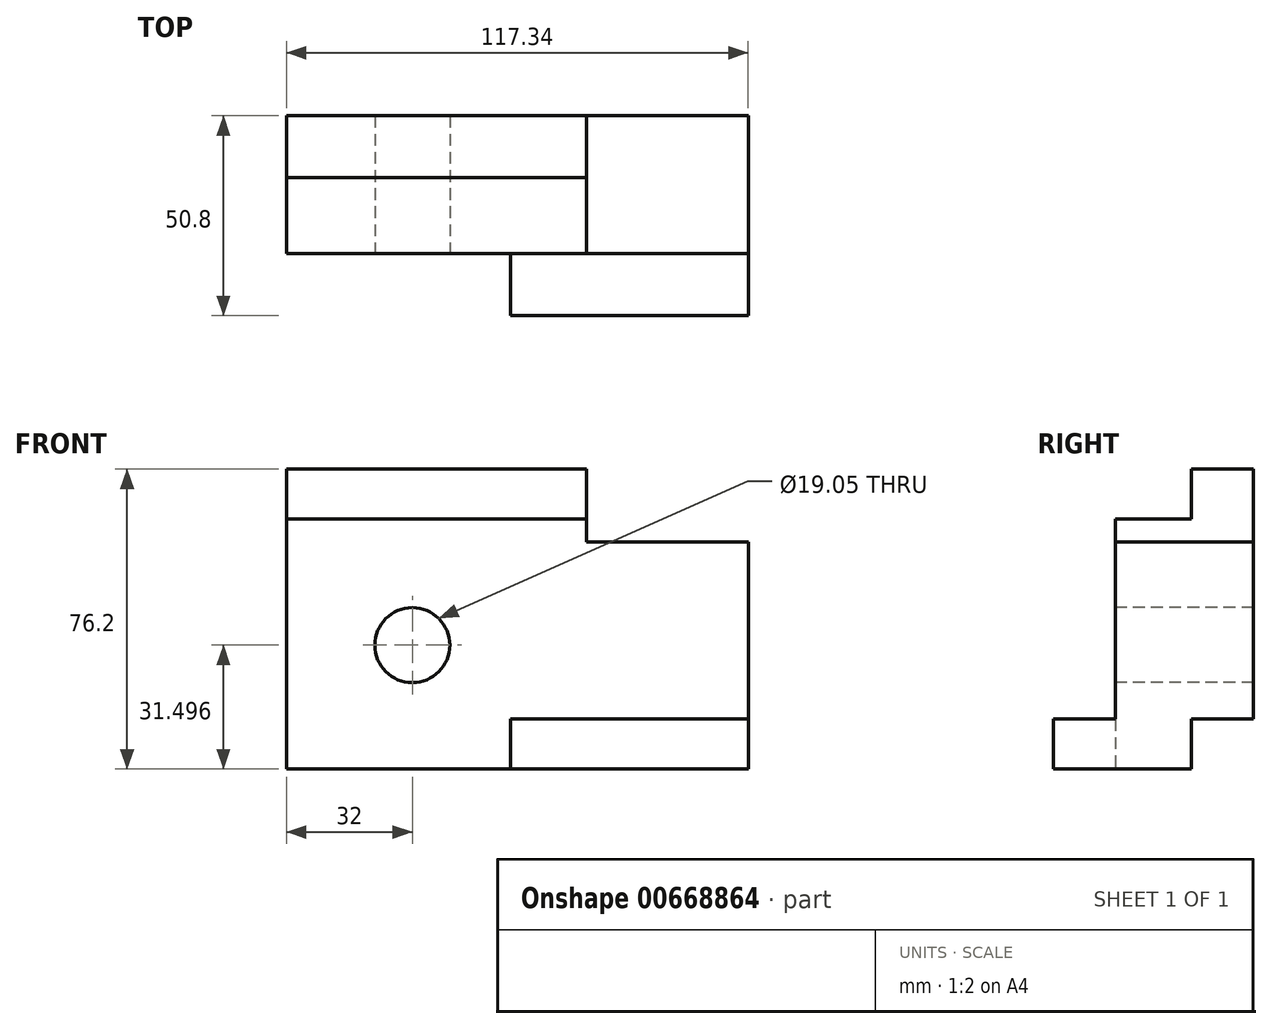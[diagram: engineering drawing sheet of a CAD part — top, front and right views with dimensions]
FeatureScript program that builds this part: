
annotation { "Feature Type Name" : "Feature", "Feature Type Description" : "" }
export const myFeature = defineFeature(function(context is Context, id is Id, definition is map)
    precondition{}
    {
        {
            var Q0;
            Q0=qCreatedBy(makeId("Front.planeOp"),FACE);
            var sketch = newSketch(context, id + "F0", { "sketchPlane" : qUnion([Q0])});
            skLineSegment(sketch, "E0.bottom", {"start": v(-58.67, 31.75) * mm, "end": v(58.67, 31.75) * mm});
            skLineSegment(sketch, "E0.top", {"start": v(-58.67, -31.75) * mm, "end": v(58.67, -31.75) * mm});
            skLineSegment(sketch, "E0.left", {"start": v(-58.67, 31.75) * mm, "end": v(-58.67, -31.75) * mm});
            skLineSegment(sketch, "E0.right", {"start": v(58.67, 31.75) * mm, "end": v(58.67, -31.75) * mm});
            skPoint(sketch, "E0.middle", {"position": v(0, 0) * mm});
            skSolve(sketch);
        }
        {
            var Q0;
            Q0=makeQuery(id+"F0.imprint","IMPRINT",FACE,{"disambiguationData":[TD([[makeQuery(id+"F0.imprint","IMPRINT",EDGE,{"derivedFrom":sQuery(id+"F0.wireOp",EDGE,"E0.bottom")}),-1.0]])]});
            extrude(context, id + "F1", {"entities" : qUnion([Q0]), "depth" : 35.05 * mm, "offsetDistance" : 25.4 * mm});
        }
        {
            var Q0;
            Q0=makeQuery(id+"F1.opExtrude","SWEPT_FACE",FACE,{"disambiguationData":[OSD([sQuery(id+"F0.wireOp",EDGE,"E0.bottom")])]});
            var sketch = newSketch(context, id + "F2", { "sketchPlane" : qUnion([Q0])});
            skLineSegment(sketch, "E1.bottom", {"start": v(-58.67, 0) * mm, "end": v(58.67, 0) * mm});
            skLineSegment(sketch, "E1.top", {"start": v(-58.67, -15.75) * mm, "end": v(58.67, -15.75) * mm});
            skLineSegment(sketch, "E1.left", {"start": v(-58.67, 0) * mm, "end": v(-58.67, -15.75) * mm});
            skLineSegment(sketch, "E1.right", {"start": v(58.67, 0) * mm, "end": v(58.67, -15.75) * mm});
            skSolve(sketch);
        }
        {
            var Q0;
            Q0=makeQuery(id+"F2.imprint","IMPRINT",FACE,{"disambiguationData":[TD([[makeQuery(id+"F2.imprint","IMPRINT",EDGE,{"derivedFrom":sQuery(id+"F2.wireOp",EDGE,"E1.bottom")}),-1.0]])]});
            extrude(context, id + "F3", {"entities" : qUnion([Q0]), "operationType" : NewBodyOperationType.ADD, "depth" : 12.7 * mm, "offsetDistance" : 25.4 * mm});
        }
        {
            var Q0;
            Q0=makeQuery(id+"F3.opExtrude","CAP_FACE",FACE,{"disambiguationData":[OSD([sQuery(id+"F2.wireOp",EDGE,"E1.bottom"),sQuery(id+"F2.wireOp",EDGE,"E1.top"),sQuery(id+"F2.wireOp",EDGE,"E1.left"),sQuery(id+"F2.wireOp",EDGE,"E1.right")])],"isStart":false});
            var sketch = newSketch(context, id + "F4", { "sketchPlane" : qUnion([Q0])});
            skLineSegment(sketch, "E2.bottom", {"start": v(58.67, 0) * mm, "end": v(17.53, 0) * mm});
            skLineSegment(sketch, "E2.top", {"start": v(58.67, -35.05) * mm, "end": v(17.53, -35.05) * mm});
            skLineSegment(sketch, "E2.left", {"start": v(58.67, 0) * mm, "end": v(58.67, -35.05) * mm});
            skLineSegment(sketch, "E2.right", {"start": v(17.53, 0) * mm, "end": v(17.53, -35.05) * mm});
            skSolve(sketch);
        }
        {
            var Q0;
            {var subQ0=sQuery(id+"F4.wireOp",EDGE,"E2.bottom");Q0=makeQuery(id+"F4.imprint","IMPRINT",FACE,{"disambiguationData":[TD([[makeQuery(id+"F4.imprint","IMPRINT",EDGE,{"derivedFrom":subQ0}),-1.0]])]});}
            var Q1;
            {var subQ0=sQuery(id+"F4.wireOp",EDGE,"E2.top");Q1=makeQuery(id+"F4.imprint","IMPRINT",FACE,{"disambiguationData":[TD([[makeQuery(id+"F4.imprint","IMPRINT",EDGE,{"derivedFrom":subQ0}),-1.0]])]});}
            extrude(context, id + "F5", {"entities" : qUnion([Q0, Q1]), "operationType" : NewBodyOperationType.REMOVE, "oppositeDirection" : true, "depth" : 18.44 * mm, "offsetDistance" : 25.4 * mm});
        }
        {
            var Q0;
            Q0=makeQuery(id+"F3.boolean.opBoolean","MERGE",FACE,{"derivedFrom":[makeQuery(id+"F1.opExtrude","SWEPT_FACE",FACE,{"disambiguationData":[OSD([sQuery(id+"F0.wireOp",EDGE,"E0.right")])]}),makeQuery(id+"F3.opExtrude","SWEPT_FACE",FACE,{"disambiguationData":[OSD([sQuery(id+"F2.wireOp",EDGE,"E1.right")])]})]});
            var sketch = newSketch(context, id + "F6", { "sketchPlane" : qUnion([Q0])});
            skLineSegment(sketch, "E3.bottom", {"start": v(0, -31.75) * mm, "end": v(-15.75, -31.75) * mm});
            skLineSegment(sketch, "E3.top", {"start": v(0, -19.05) * mm, "end": v(-15.75, -19.05) * mm});
            skLineSegment(sketch, "E3.left", {"start": v(0, -31.75) * mm, "end": v(0, -19.05) * mm});
            skLineSegment(sketch, "E3.right", {"start": v(-15.75, -31.75) * mm, "end": v(-15.75, -19.05) * mm});
            skSolve(sketch);
        }
        {
            var Q0;
            Q0=makeQuery(id+"F6.imprint","IMPRINT",FACE,{"disambiguationData":[TD([[makeQuery(id+"F6.imprint","IMPRINT",EDGE,{"derivedFrom":sQuery(id+"F6.wireOp",EDGE,"E3.bottom")}),1.0]])]});
            extrude(context, id + "F7", {"entities" : qUnion([Q0]), "operationType" : NewBodyOperationType.REMOVE, "endBound" : BoundingType.THROUGH_ALL, "oppositeDirection" : true, "depth" : 25.4 * mm, "offsetDistance" : 25.4 * mm});
        }
        {
            var Q0;
            Q0=makeQuery(id+"F3.boolean.opBoolean","MERGE",FACE,{"derivedFrom":[makeQuery(id+"F1.opExtrude","SWEPT_FACE",FACE,{"disambiguationData":[OSD([sQuery(id+"F0.wireOp",EDGE,"E0.right")])]}),makeQuery(id+"F3.opExtrude","SWEPT_FACE",FACE,{"disambiguationData":[OSD([sQuery(id+"F2.wireOp",EDGE,"E1.right")])]})]});
            var sketch = newSketch(context, id + "F8", { "sketchPlane" : qUnion([Q0])});
            skLineSegment(sketch, "E4.bottom", {"start": v(-15.75, -31.75) * mm, "end": v(-50.8, -31.75) * mm});
            skLineSegment(sketch, "E4.top", {"start": v(-15.75, -19.05) * mm, "end": v(-50.8, -19.05) * mm});
            skLineSegment(sketch, "E4.left", {"start": v(-15.75, -31.75) * mm, "end": v(-15.75, -19.05) * mm});
            skLineSegment(sketch, "E4.right", {"start": v(-50.8, -31.75) * mm, "end": v(-50.8, -19.05) * mm});
            skSolve(sketch);
        }
        {
            var Q0;
            {var subQ3=sQuery(id+"F8.wireOp",EDGE,"E4.right");Q0=makeQuery(id+"F8.imprint","IMPRINT",FACE,{"disambiguationData":[TD([[makeQuery(id+"F8.imprint","IMPRINT",EDGE,{"derivedFrom":subQ3}),-1.0]])]});}
            extrude(context, id + "F9", {"entities" : qUnion([Q0]), "operationType" : NewBodyOperationType.ADD, "oppositeDirection" : true, "depth" : 60.45 * mm, "offsetDistance" : 25.4 * mm});
        }
        {
            var Q0;
            Q0=makeQuery(id+"F1.opExtrude","CAP_FACE",FACE,{"disambiguationData":[OSD([sQuery(id+"F0.wireOp",EDGE,"E0.bottom"),sQuery(id+"F0.wireOp",EDGE,"E0.top"),sQuery(id+"F0.wireOp",EDGE,"E0.left"),sQuery(id+"F0.wireOp",EDGE,"E0.right")])],"isStart":false});
            var sketch = newSketch(context, id + "F10", { "sketchPlane" : qUnion([Q0])});
            skCircle(sketch, "E5", {"center": v(-26.67, -0.25) * mm, "radius": 9.53 * mm});
            skSolve(sketch);
        }
        {
            var Q0;
            Q0=makeQuery(id+"F10.imprint","IMPRINT",FACE,{"disambiguationData":[TD([[makeQuery(id+"F10.imprint","IMPRINT",EDGE,{"derivedFrom":sQuery(id+"F10.wireOp",EDGE,"E5")}),1.0]])]});
            extrude(context, id + "F11", {"entities" : qUnion([Q0]), "operationType" : NewBodyOperationType.REMOVE, "endBound" : BoundingType.THROUGH_ALL, "oppositeDirection" : true, "depth" : 25.4 * mm, "offsetDistance" : 25.4 * mm});
        }
    });
